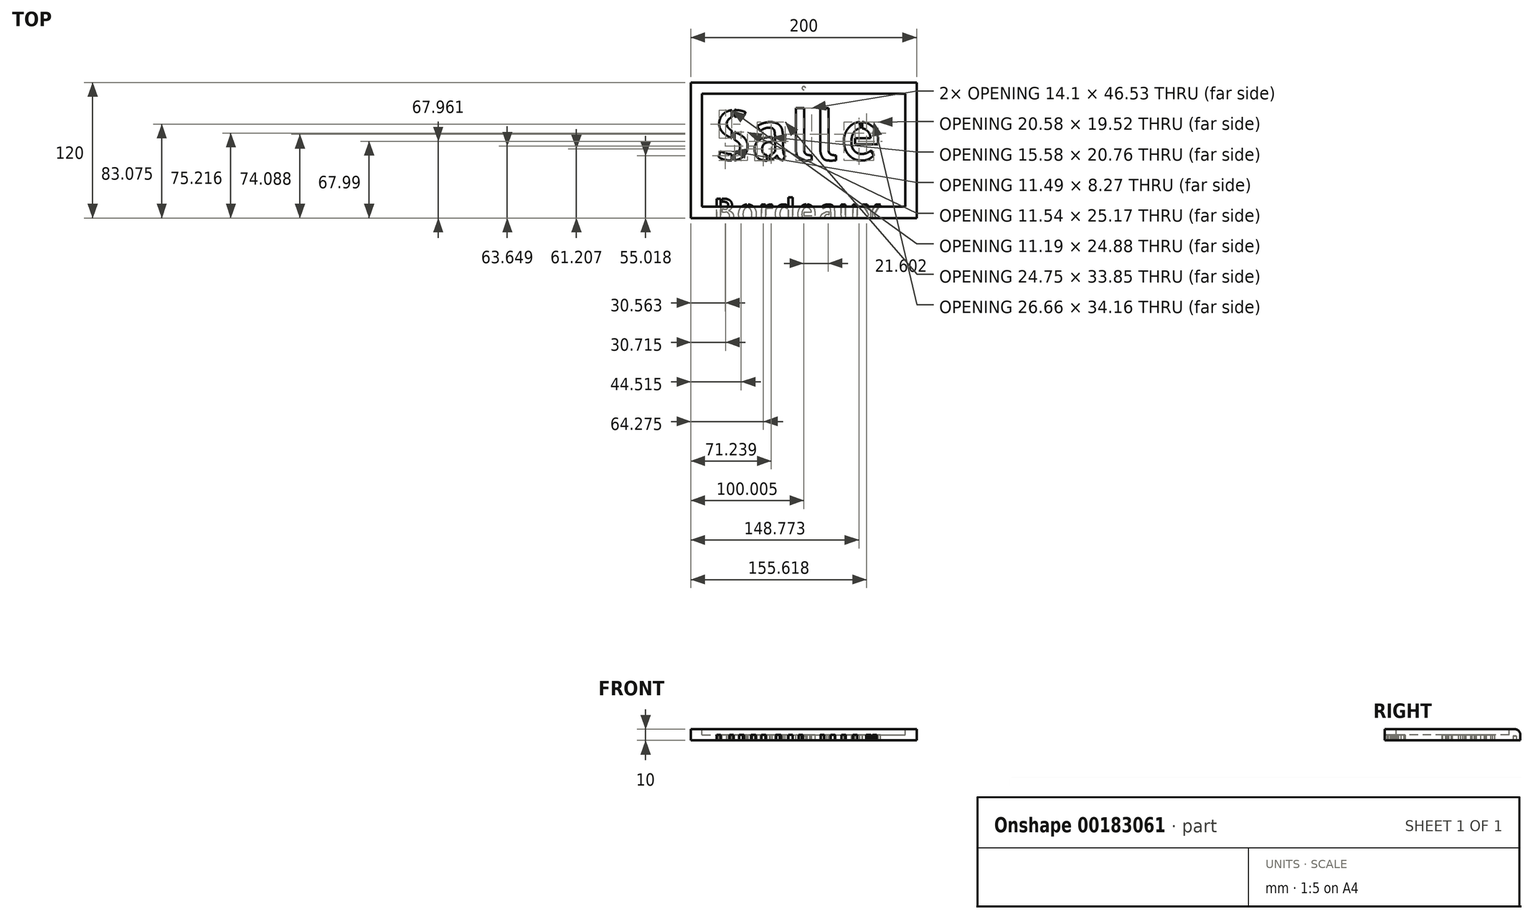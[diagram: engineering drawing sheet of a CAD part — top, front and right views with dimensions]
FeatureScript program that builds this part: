
annotation { "Feature Type Name" : "Feature", "Feature Type Description" : "" }
export const myFeature = defineFeature(function(context is Context, id is Id, definition is map)
    precondition{}
    {
        {
            var Q0;
            Q0=qCreatedBy(makeId("Top.planeOp"),FACE);
            var sketch = newSketch(context, id + "F0", { "sketchPlane" : qUnion([Q0])});
            skLineSegment(sketch, "E0.bottom", {"start": v(-96.22, 56.75) * mm, "end": v(103.78, 56.75) * mm});
            skLineSegment(sketch, "E0.top", {"start": v(-96.22, -63.25) * mm, "end": v(103.78, -63.25) * mm});
            skLineSegment(sketch, "E0.left", {"start": v(-96.22, 56.75) * mm, "end": v(-96.22, -63.25) * mm});
            skLineSegment(sketch, "E0.right", {"start": v(103.78, 56.75) * mm, "end": v(103.78, -63.25) * mm});
            skSolve(sketch);
        }
        {
            var Q0;
            Q0=makeQuery(id+"F0.imprint","IMPRINT",FACE,{"disambiguationData":[TD([[makeQuery(id+"F0.imprint","IMPRINT",EDGE,{"derivedFrom":sQuery(id+"F0.wireOp",EDGE,"E0.bottom")}),-1.0]])]});
            extrude(context, id + "F1", {"entities" : qUnion([Q0]), "depth" : 10 * mm});
        }
        {
            var Q0;
            Q0=makeQuery(id+"F1.opExtrude","CAP_FACE",FACE,{"disambiguationData":[OSD([sQuery(id+"F0.wireOp",EDGE,"E0.bottom"),sQuery(id+"F0.wireOp",EDGE,"E0.top"),sQuery(id+"F0.wireOp",EDGE,"E0.left"),sQuery(id+"F0.wireOp",EDGE,"E0.right")])],"isStart":false});
            var sketch = newSketch(context, id + "F2", { "sketchPlane" : qUnion([Q0])});
            skLineSegment(sketch, "E1.bottom", {"start": v(-86.22, 46.75) * mm, "end": v(93.78, 46.75) * mm});
            skLineSegment(sketch, "E1.top", {"start": v(-86.22, -53.25) * mm, "end": v(93.78, -53.25) * mm});
            skLineSegment(sketch, "E1.left", {"start": v(-86.22, 46.75) * mm, "end": v(-86.22, -53.25) * mm});
            skLineSegment(sketch, "E1.right", {"start": v(93.78, 46.75) * mm, "end": v(93.78, -53.25) * mm});
            skSolve(sketch);
        }
        {
            var Q0;
            Q0=makeQuery(id+"F2.imprint","IMPRINT",FACE,{"disambiguationData":[TD([[makeQuery(id+"F2.imprint","IMPRINT",EDGE,{"derivedFrom":sQuery(id+"F2.wireOp",EDGE,"E1.bottom")}),-1.0]])]});
            extrude(context, id + "F3", {"entities" : qUnion([Q0]), "operationType" : NewBodyOperationType.REMOVE, "oppositeDirection" : true, "depth" : 5 * mm});
        }
        {
            var Q0;
            Q0=makeQuery(id+"F3.boolean.opBoolean","COPY",FACE,{"derivedFrom":makeQuery(id+"F3.opExtrude","CAP_FACE",FACE,{"disambiguationData":[OSD([sQuery(id+"F2.wireOp",EDGE,"E1.bottom"),sQuery(id+"F2.wireOp",EDGE,"E1.top"),sQuery(id+"F2.wireOp",EDGE,"E1.left"),sQuery(id+"F2.wireOp",EDGE,"E1.right")])],"isStart":false})});
            var sketch = newSketch(context, id + "F4", { "sketchPlane" : qUnion([Q0])});
            skText(sketch, "E2", { "text": "Salle", "fontName": "AllertaStencil-Regular.ttf"});
            skText(sketch, "E3", { "text": "Bordeaux", "fontName": "AllertaStencil-Regular.ttf"});
            const initialGuessF4  = {"E2": [-0.07622, -0.01213, 1, 0, 0.04387], "E3": [-0.07622, -0.06825, 1, 0, 0.02216]};
            skSetInitialGuess(sketch, initialGuessF4);
            skSolve(sketch);
        }
        {
            var Q0;
            Q0 = qSketchRegion(id + "F4", true);
            var Q1;
            Q1=makeQuery(id+"F1.opExtrude","CAP_FACE",FACE,{"disambiguationData":[OSD([sQuery(id+"F0.wireOp",EDGE,"E0.bottom"),sQuery(id+"F0.wireOp",EDGE,"E0.top"),sQuery(id+"F0.wireOp",EDGE,"E0.left"),sQuery(id+"F0.wireOp",EDGE,"E0.right")])],"isStart":true});
            extrude(context, id + "F5", {"entities" : qUnion([Q0]), "operationType" : NewBodyOperationType.REMOVE, "endBound" : BoundingType.UP_TO_SURFACE, "oppositeDirection" : true, "endBoundEntityFace" : qUnion([Q1]), "depth" : 25 * mm});
        }
        {
            var Q0;
            Q0=makeQuery(id+"F1.opExtrude","CAP_FACE",FACE,{"disambiguationData":[OSD([sQuery(id+"F0.wireOp",EDGE,"E0.bottom"),sQuery(id+"F0.wireOp",EDGE,"E0.top"),sQuery(id+"F0.wireOp",EDGE,"E0.left"),sQuery(id+"F0.wireOp",EDGE,"E0.right")])],"isStart":true});
            var sketch = newSketch(context, id + "F6", { "sketchPlane" : qUnion([Q0])});
            skCircle(sketch, "E4", {"center": v(3.78, -51.75) * mm, "radius": 1.5 * mm});
            skSolve(sketch);
        }
        {
            var Q0;
            Q0 = qSketchRegion(id + "F6", true);
            extrude(context, id + "F7", {"entities" : qUnion([Q0]), "operationType" : NewBodyOperationType.REMOVE, "oppositeDirection" : true, "depth" : 4 * mm});
        }
        {
            var Q0;
            Q0=makeQuery(id+"F1.opExtrude","CAP_EDGE",EDGE,{"disambiguationData":[OSD([sQuery(id+"F0.wireOp",EDGE,"E0.bottom")])],"isStart":false});
            fillet(context, id + "F8", {"entities" : qUnion([Q0]), "radius" : 5 * mm, "tangentPropagation" : true, "allowEdgeOverflow" : false});
        }
    });
